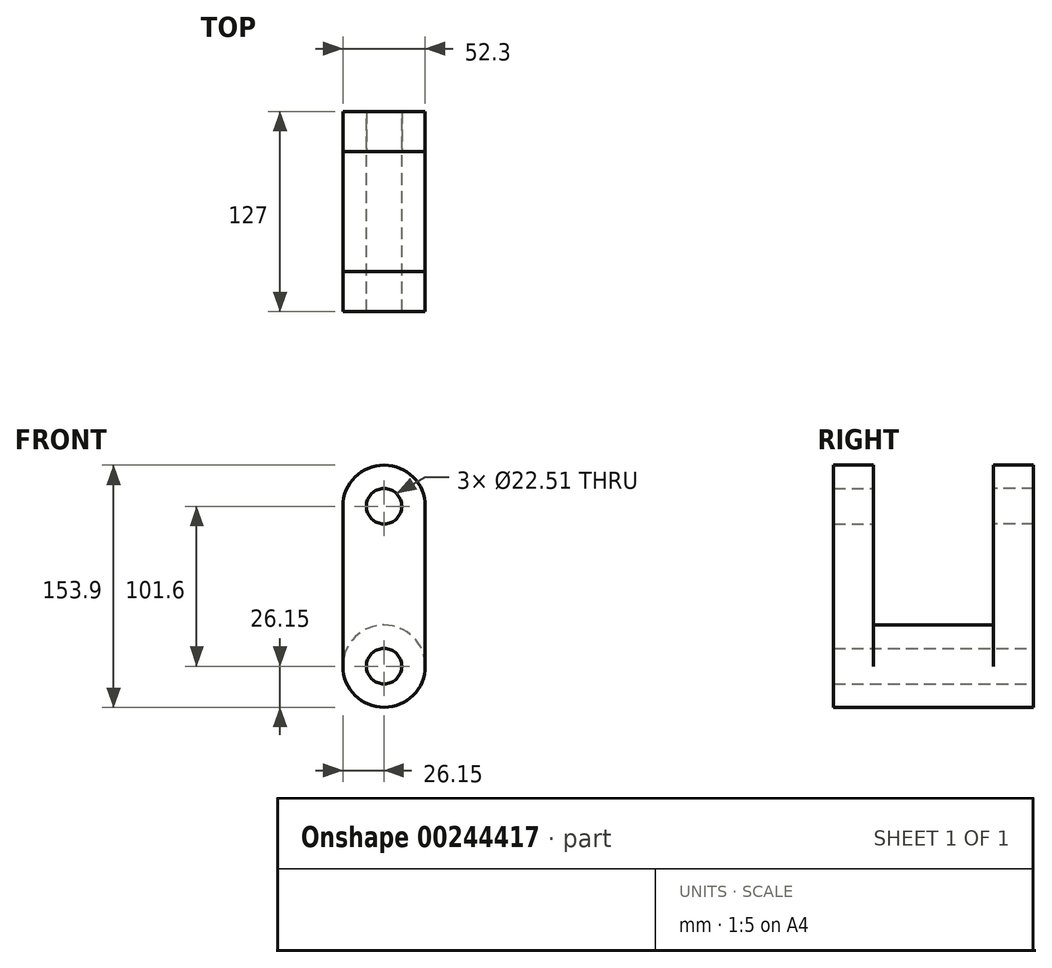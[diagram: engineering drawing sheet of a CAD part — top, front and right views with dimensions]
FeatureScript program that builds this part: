
annotation { "Feature Type Name" : "Feature", "Feature Type Description" : "" }
export const myFeature = defineFeature(function(context is Context, id is Id, definition is map)
    precondition{}
    {
        {
            var Q0;
            Q0=qCreatedBy(makeId("Front.planeOp"),FACE);
            var sketch = newSketch(context, id + "F0", { "sketchPlane" : qUnion([Q0])});
            skCircle(sketch, "E0", {"center": v(0, 0) * mm, "radius": 26.15 * mm});
            skCircle(sketch, "E1", {"center": v(0, 0) * mm, "radius": 11.26 * mm});
            skSolve(sketch);
        }
        {
            var Q0;
            Q0=makeQuery(id+"F0.imprint","IMPRINT",FACE,{"disambiguationData":[TD([[makeQuery(id+"F0.imprint","IMPRINT",EDGE,{"derivedFrom":sQuery(id+"F0.wireOp",EDGE,"E0")}),1.0]])]});
            extrude(context, id + "F1", {"entities" : qUnion([Q0]), "depth" : 38.1 * mm});
        }
        {
            var Q0;
            Q0=makeQuery(id+"F1.opExtrude","CAP_FACE",FACE,{"disambiguationData":[OSD([sQuery(id+"F0.wireOp",EDGE,"E0"),sQuery(id+"F0.wireOp",EDGE,"E1")])],"isStart":true});
            extrude(context, id + "F2", {"entities" : qUnion([Q0]), "operationType" : NewBodyOperationType.ADD, "depth" : 38.1 * mm});
        }
        {
            var Q0;
            Q0=makeQuery(id+"F1.opExtrude","CAP_FACE",FACE,{"disambiguationData":[OSD([sQuery(id+"F0.wireOp",EDGE,"E0"),sQuery(id+"F0.wireOp",EDGE,"E1")])],"isStart":false});
            var sketch = newSketch(context, id + "F3", { "sketchPlane" : qUnion([Q0])});
            skLineSegment(sketch, "E2", {"start": v(26.15, 0) * mm, "end": v(26.15, 101.6) * mm});
            skLineSegment(sketch, "E3", {"start": v(-26.15, 0) * mm, "end": v(-26.15, 101.6) * mm});
            skArc(sketch, "E4", {"start": v(26.15, 101.6) * mm, "mid": v(0, 127.75) * mm, "end": v(-26.15, 101.6) * mm});
            skCircle(sketch, "E5", {"center": v(0, 101.6) * mm, "radius": 11.26 * mm});
            skSolve(sketch);
        }
        {
            var Q0;
            Q0=makeQuery(id+"F2.opExtrude","CAP_FACE",FACE,{"disambiguationData":[OSD([sQuery(id+"F0.wireOp",EDGE,"E0"),sQuery(id+"F0.wireOp",EDGE,"E1")])],"isStart":false});
            var sketch = newSketch(context, id + "F4", { "sketchPlane" : qUnion([Q0])});
            skLineSegment(sketch, "E6", {"start": v(26.15, 0) * mm, "end": v(26.15, 101.6) * mm});
            skLineSegment(sketch, "E7", {"start": v(-26.15, 0) * mm, "end": v(-26.15, 101.6) * mm});
            skArc(sketch, "E8", {"start": v(26.15, 101.6) * mm, "mid": v(0, 127.75) * mm, "end": v(-26.15, 101.6) * mm});
            skCircle(sketch, "E9", {"center": v(0, 101.6) * mm, "radius": 11.26 * mm});
            skSolve(sketch);
        }
        {
            var Q0;
            {var subQ1=sQuery(id+"F3.wireOp",EDGE,"E2");Q0=makeQuery(id+"F3.imprint","IMPRINT",FACE,{"disambiguationData":[TD([[makeQuery(id+"F3.imprint","IMPRINT",EDGE,{"derivedFrom":subQ1}),1.0]])]});}
            var Q1;
            Q1=makeQuery(id+"F3.imprint","IMPRINT",FACE,{"disambiguationData":[TD([[makeQuery(id+"F3.imprint","IMPRINT",EDGE,{"derivedFrom":makeQuery(id+"F1.opExtrude","CAP_EDGE",EDGE,{"disambiguationData":[OSD([sQuery(id+"F0.wireOp",EDGE,"E1")])],"isStart":false})}),-1.0]])]});
            extrude(context, id + "F5", {"entities" : qUnion([Q0, Q1]), "operationType" : NewBodyOperationType.ADD, "depth" : 25.4 * mm});
        }
        {
            var Q0;
            {var subQ0=sQuery(id+"F4.wireOp",EDGE,"E6");Q0=makeQuery(id+"F4.imprint","IMPRINT",FACE,{"disambiguationData":[TD([[makeQuery(id+"F4.imprint","IMPRINT",EDGE,{"derivedFrom":subQ0}),1.0]])]});}
            var Q1;
            Q1=makeQuery(id+"F4.imprint","IMPRINT",FACE,{"disambiguationData":[TD([[makeQuery(id+"F4.imprint","IMPRINT",EDGE,{"derivedFrom":makeQuery(id+"F2.opExtrude","CAP_EDGE",EDGE,{"disambiguationData":[OSD([sQuery(id+"F0.wireOp",EDGE,"E1")])],"isStart":false})}),1.0]])]});
            extrude(context, id + "F6", {"entities" : qUnion([Q0, Q1]), "operationType" : NewBodyOperationType.ADD, "depth" : 25.4 * mm});
        }
    });
